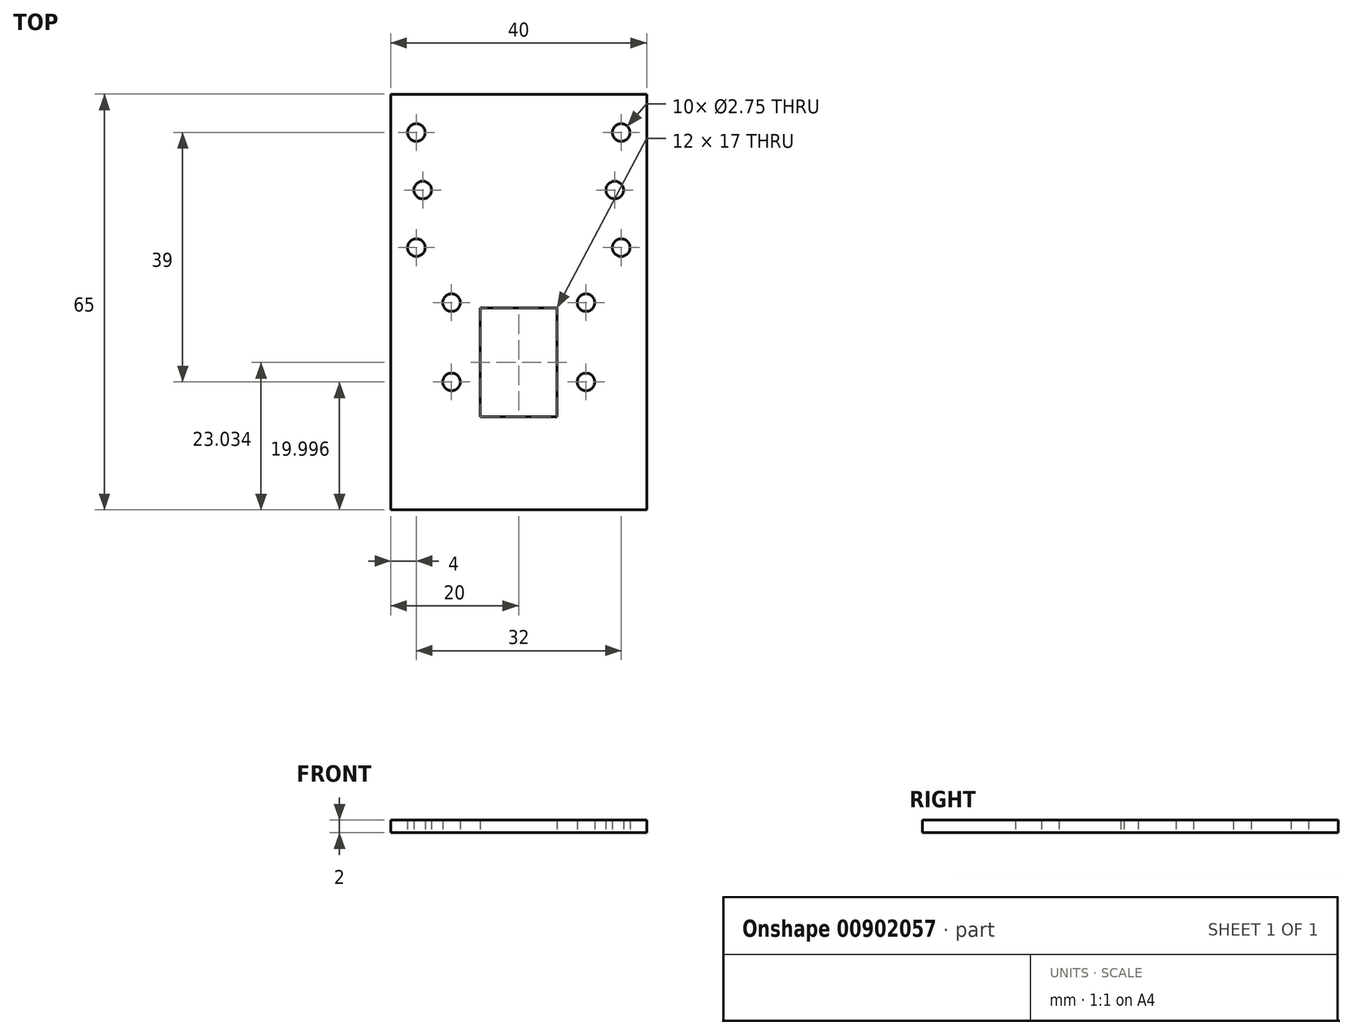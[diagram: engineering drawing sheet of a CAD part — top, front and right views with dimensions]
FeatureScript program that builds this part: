
annotation { "Feature Type Name" : "Feature", "Feature Type Description" : "" }
export const myFeature = defineFeature(function(context is Context, id is Id, definition is map)
    precondition{}
    {
        {
            var Q0;
            Q0=qCreatedBy(makeId("Top.planeOp"),FACE);
            var sketch = newSketch(context, id + "F0", { "sketchPlane" : qUnion([Q0])});
            skLineSegment(sketch, "E0.bottom", {"start": v(20, -63.95) * mm, "end": v(0, -63.95) * mm});
            skLineSegment(sketch, "E0.left", {"start": v(20, -63.95) * mm, "end": v(20, 1.05) * mm});
            skLineSegment(sketch, "E0.right", {"start": v(-20, -63.95) * mm, "end": v(-20, 1.05) * mm});
            skCircle(sketch, "E1", {"center": v(10.5, -43.95) * mm, "radius": 1.38 * mm});
            skLineSegment(sketch, "E2", {"start": v(0, -32.42) * mm, "end": v(6, -32.42) * mm});
            skLineSegment(sketch, "E3.MirrorCS", {"start": v(0, -32.42) * mm, "end": v(-6, -32.42) * mm});
            skLineSegment(sketch, "E4", {"start": v(-6, -32.42) * mm, "end": v(-6, -49.42) * mm});
            skLineSegment(sketch, "E5", {"start": v(-6, -49.42) * mm, "end": v(6, -49.42) * mm});
            skLineSegment(sketch, "E6", {"start": v(6, -32.42) * mm, "end": v(6, -49.42) * mm});
            skCircle(sketch, "E7", {"center": v(-10.5, -31.55) * mm, "radius": 1.38 * mm});
            skLineSegment(sketch, "E8", {"start": v(0, -32.42) * mm, "end": v(0, -30.84) * mm});
            skCircle(sketch, "E9.MirrorC", {"center": v(10.5, -31.55) * mm, "radius": 1.38 * mm});
            skCircle(sketch, "E10", {"center": v(-10.5, -43.95) * mm, "radius": 1.38 * mm});
            skLineSegment(sketch, "E11", {"start": v(0, -63.95) * mm, "end": v(-20, -63.95) * mm});
            skPoint(sketch, "E12.endSnap0", {"position": v(10, -63.95) * mm});
            skLineSegment(sketch, "E13", {"start": v(20, 1.05) * mm, "end": v(-20, 1.05) * mm});
            skCircle(sketch, "E14.MirrorC", {"center": v(-16, -4.95) * mm, "radius": 1.38 * mm});
            skCircle(sketch, "E15.MirrorC", {"center": v(16, -4.95) * mm, "radius": 1.38 * mm});
            skCircle(sketch, "E16.MirrorC", {"center": v(-15, -13.95) * mm, "radius": 1.38 * mm});
            skCircle(sketch, "E17.MirrorC", {"center": v(15, -13.95) * mm, "radius": 1.38 * mm});
            skCircle(sketch, "E18.MirrorC", {"center": v(16, -22.95) * mm, "radius": 1.38 * mm});
            skCircle(sketch, "E19.MirrorC", {"center": v(-16, -22.95) * mm, "radius": 1.38 * mm});
            skLineSegment(sketch, "E20", {"start": v(15, -13.95) * mm, "end": v(15, -4.95) * mm});
            skLineSegment(sketch, "E21", {"start": v(16, -4.95) * mm, "end": v(16, 1.05) * mm});
            skLineSegment(sketch, "E22", {"start": v(-16, -22.95) * mm, "end": v(-16, 1.05) * mm});
            skSolve(sketch);
        }
        {
            var Q0;
            {var subQ3=sQuery(id+"F0.wireOp",EDGE,"E0.bottom");Q0=makeQuery(id+"F0.imprint","IMPRINT",FACE,{"disambiguationData":[TD([[makeQuery(id+"F0.imprint","IMPRINT",EDGE,{"derivedFrom":subQ3}),-1.0]])]});}
            extrude(context, id + "F1", {"entities" : qUnion([Q0]), "depth" : 2 * mm, "offsetDistance" : 25 * mm});
        }
    });
